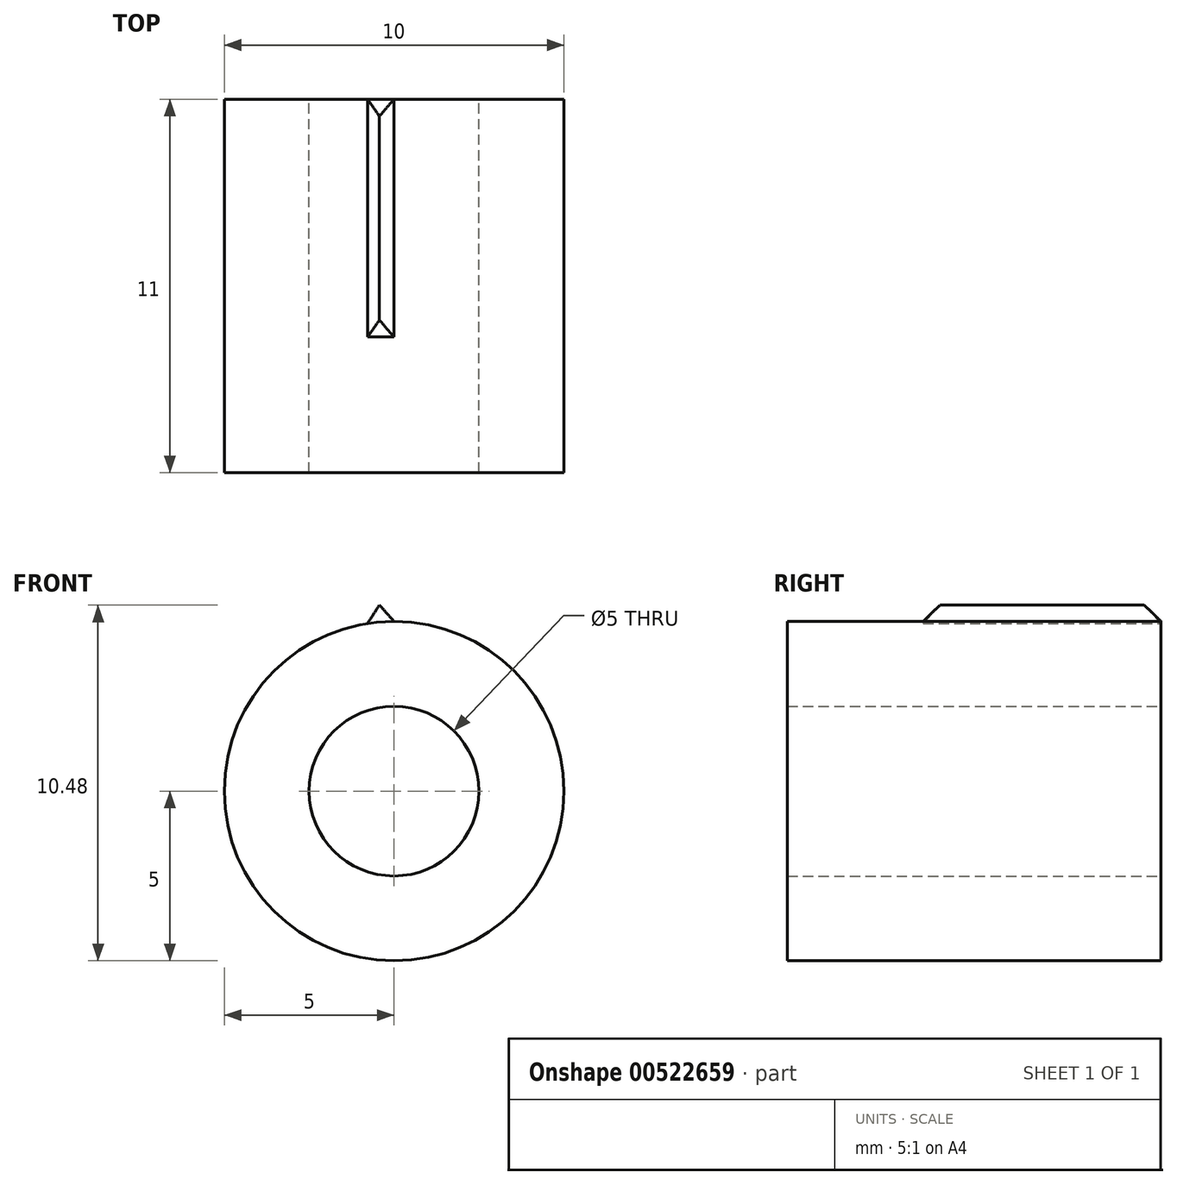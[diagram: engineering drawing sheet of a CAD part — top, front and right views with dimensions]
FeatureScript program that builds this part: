
annotation { "Feature Type Name" : "Feature", "Feature Type Description" : "" }
export const myFeature = defineFeature(function(context is Context, id is Id, definition is map)
    precondition{}
    {
        {
            var Q0;
            Q0=qCreatedBy(makeId("Front.planeOp"),FACE);
            var sketch = newSketch(context, id + "F0", { "sketchPlane" : qUnion([Q0])});
            skCircle(sketch, "E0", {"center": v(0, 0) * mm, "radius": 5.5 * mm, "construction": true});
            skCircle(sketch, "E1", {"center": v(0, 0) * mm, "radius": 5 * mm});
            skLineSegment(sketch, "E2", {"start": v(0, 0) * mm, "end": v(0, 5.5) * mm, "construction": true});
            skLineSegment(sketch, "E3", {"start": v(0, 0) * mm, "end": v(-0.86, 5.43) * mm, "construction": true});
            skLineSegment(sketch, "E4", {"start": v(0, 0) * mm, "end": v(-0.43, 5.48) * mm, "construction": true});
            skLineSegment(sketch, "E5", {"start": v(0, 5) * mm, "end": v(-0.43, 5.48) * mm});
            skLineSegment(sketch, "E6", {"start": v(-0.43, 5.48) * mm, "end": v(-0.78, 4.94) * mm});
            skCircle(sketch, "E7", {"center": v(0, 0) * mm, "radius": 2.5 * mm});
            skSolve(sketch);
        }
        {
            var Q0;
            {var subQ0=sQuery(id+"F0.wireOp",EDGE,"E1");var subQ1=makeQuery(id+"F0.imprint","INTERSECT",VERTEX,{"derivedFrom":[subQ0,sQuery(id+"F0.wireOp",EDGE,"E5")]});Q0=makeQuery(id+"F0.imprint","IMPRINT",FACE,{"disambiguationData":[TD([[makeQuery(id+"F0.imprint","IMPRINT",EDGE,{"disambiguationData":[TD([[subQ1,-1.0]])],"derivedFrom":subQ0}),1.0]])]});}
            extrude(context, id + "F1", {"entities" : qUnion([Q0]), "depth" : 11 * mm, "offsetDistance" : 25 * mm});
        }
        {
            var Q0;
            {var subQ0=sQuery(id+"F0.wireOp",EDGE,"E5");Q0=makeQuery(id+"F0.imprint","IMPRINT",FACE,{"disambiguationData":[TD([[makeQuery(id+"F0.imprint","IMPRINT",EDGE,{"derivedFrom":subQ0}),1.0]])]});}
            extrude(context, id + "F2", {"entities" : qUnion([Q0]), "operationType" : NewBodyOperationType.ADD, "depth" : 7 * mm, "offsetDistance" : 25 * mm});
        }
        {
            var Q0;
            Q0=qCreatedBy(makeId("Top.planeOp"),FACE);
            var sketch = newSketch(context, id + "F3", { "sketchPlane" : qUnion([Q0])});
            skLineSegment(sketch, "E8", {"start": v(0, 0) * mm, "end": v(0, -15.45) * mm, "construction": true});
            skLineSegment(sketch, "E9", {"start": v(5, 0) * mm, "end": v(7, -2) * mm});
            skLineSegment(sketch, "E10", {"start": v(7, -2) * mm, "end": v(7, -5) * mm});
            skLineSegment(sketch, "E11", {"start": v(7, -5) * mm, "end": v(5, -7) * mm});
            skLineSegment(sketch, "E12.0", {"start": v(5, 0) * mm, "end": v(-5, 0) * mm, "construction": true});
            skLineSegment(sketch, "E13", {"start": v(5, 0) * mm, "end": v(8, 0) * mm});
            skLineSegment(sketch, "E14", {"start": v(8, 0) * mm, "end": v(8, -7) * mm});
            skLineSegment(sketch, "E15", {"start": v(8, -7) * mm, "end": v(5, -7) * mm});
            skSolve(sketch);
        }
        {
            var Q0;
            Q0=qSketchRegion(id+"F3",true);
            var Q1;
            Q1=sQuery(id+"F3.wireOp",EDGE,"E8");
            revolve(context, id + "F4", {"operationType" : NewBodyOperationType.REMOVE, "entities" : qUnion([Q0]), "axis" : qUnion([Q1]), "revolveType" : RevolveType.FULL, "oppositeDirection" : true});
        }
    });
